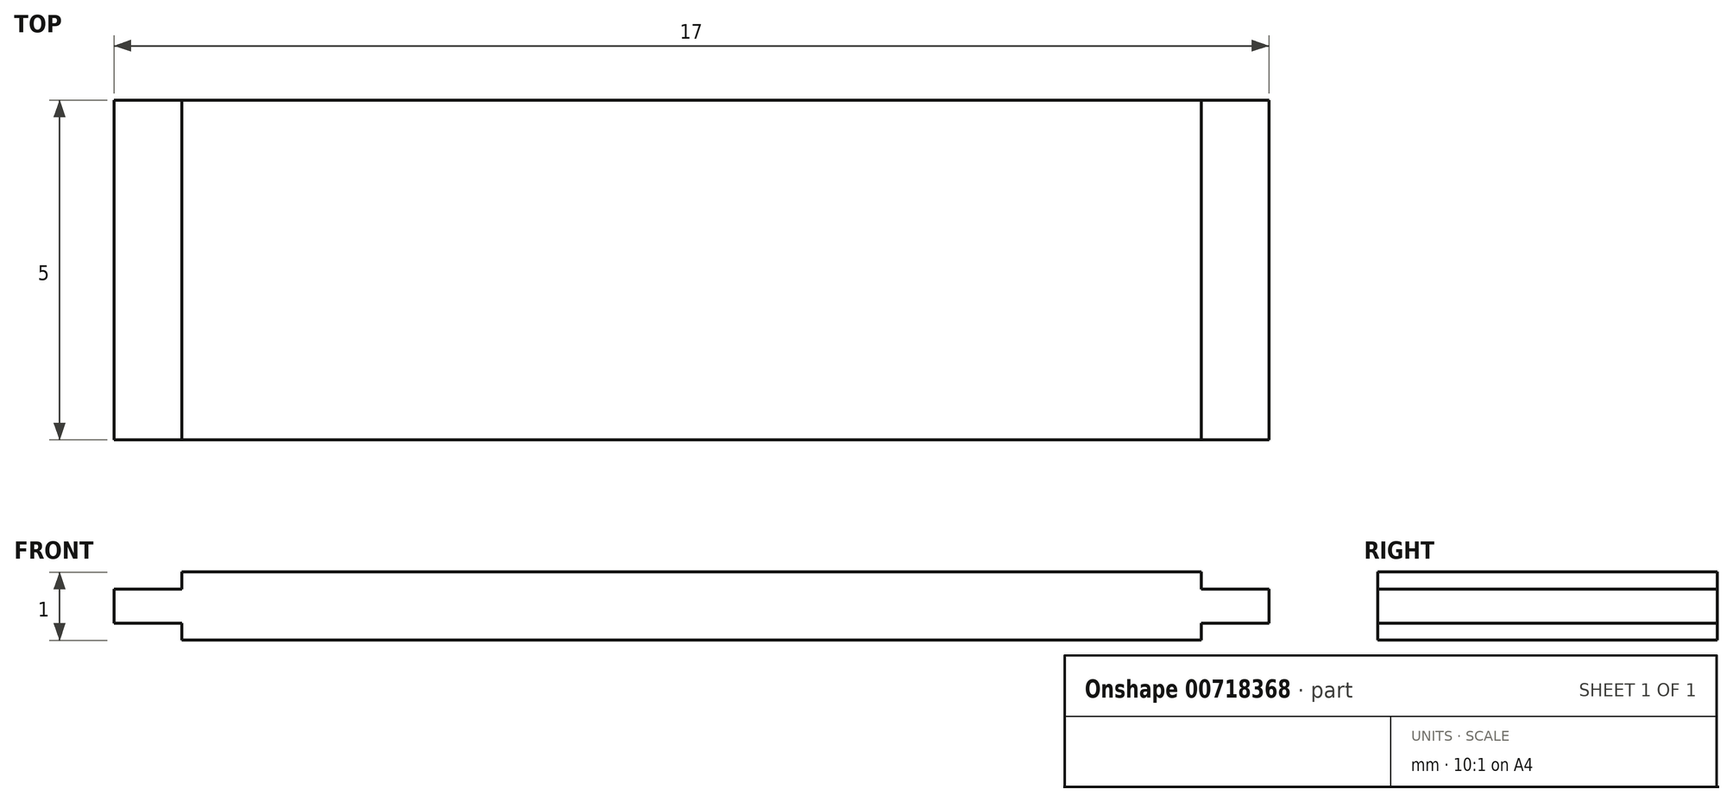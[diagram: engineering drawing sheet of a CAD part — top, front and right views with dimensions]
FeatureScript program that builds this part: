
annotation { "Feature Type Name" : "Feature", "Feature Type Description" : "" }
export const myFeature = defineFeature(function(context is Context, id is Id, definition is map)
    precondition{}
    {
        {
            var Q0;
            Q0=qCreatedBy(makeId("Front.planeOp"),FACE);
            var sketch = newSketch(context, id + "F0", { "sketchPlane" : qUnion([Q0])});
            skLineSegment(sketch, "E0.bottom", {"start": v(-2.69, -4.7) * mm, "end": v(-17.69, -4.7) * mm});
            skLineSegment(sketch, "E0.top", {"start": v(-2.69, -5.7) * mm, "end": v(-17.69, -5.7) * mm});
            skLineSegment(sketch, "E0.left", {"start": v(-2.69, -4.7) * mm, "end": v(-2.69, -5.7) * mm});
            skLineSegment(sketch, "E0.right", {"start": v(-17.69, -4.7) * mm, "end": v(-17.69, -5.7) * mm});
            skSolve(sketch);
        }
        {
            var Q0;
            Q0=makeQuery(id+"F0.imprint","IMPRINT",FACE,{"disambiguationData":[TD([[makeQuery(id+"F0.imprint","IMPRINT",EDGE,{"derivedFrom":sQuery(id+"F0.wireOp",EDGE,"E0.bottom")}),1.0]])]});
            extrude(context, id + "F1", {"entities" : qUnion([Q0]), "depth" : 5 * mm, "offsetDistance" : 25 * mm});
        }
        {
            var Q0;
            Q0=makeQuery(id+"F1.opExtrude","SWEPT_FACE",FACE,{"disambiguationData":[OSD([sQuery(id+"F0.wireOp",EDGE,"E0.right")])]});
            var sketch = newSketch(context, id + "F2", { "sketchPlane" : qUnion([Q0])});
            skLineSegment(sketch, "E1", {"start": v(0, -4.7) * mm, "end": v(0, -4.95) * mm});
            skLineSegment(sketch, "E2", {"start": v(0, -5.7) * mm, "end": v(0, -5.45) * mm});
            skLineSegment(sketch, "E3.bottom", {"start": v(0, -4.95) * mm, "end": v(5, -4.95) * mm});
            skLineSegment(sketch, "E3.top", {"start": v(0, -5.45) * mm, "end": v(5, -5.45) * mm});
            skLineSegment(sketch, "E3.left", {"start": v(0, -4.95) * mm, "end": v(0, -5.45) * mm});
            skLineSegment(sketch, "E3.right", {"start": v(5, -4.95) * mm, "end": v(5, -5.45) * mm});
            skSolve(sketch);
        }
        {
            var Q0;
            Q0=makeQuery(id+"F2.imprint","IMPRINT",FACE,{"disambiguationData":[TD([[makeQuery(id+"F2.imprint","IMPRINT",EDGE,{"derivedFrom":sQuery(id+"F2.wireOp",EDGE,"E3.bottom")}),-1.0]])]});
            extrude(context, id + "F3", {"entities" : qUnion([Q0]), "operationType" : NewBodyOperationType.ADD, "depth" : 1 * mm, "offsetDistance" : 25 * mm});
        }
        {
            var Q0;
            Q0=makeQuery(id+"F1.opExtrude","SWEPT_FACE",FACE,{"disambiguationData":[OSD([sQuery(id+"F0.wireOp",EDGE,"E0.left")])]});
            var sketch = newSketch(context, id + "F4", { "sketchPlane" : qUnion([Q0])});
            skLineSegment(sketch, "E4.bottom", {"start": v(-5, -4.95) * mm, "end": v(0, -4.95) * mm});
            skLineSegment(sketch, "E4.top", {"start": v(-5, -5.45) * mm, "end": v(0, -5.45) * mm});
            skLineSegment(sketch, "E4.left", {"start": v(-5, -4.95) * mm, "end": v(-5, -5.45) * mm});
            skLineSegment(sketch, "E4.right", {"start": v(0, -4.95) * mm, "end": v(0, -5.45) * mm});
            skSolve(sketch);
        }
        {
            var Q0;
            Q0=makeQuery(id+"F4.imprint","IMPRINT",FACE,{"disambiguationData":[TD([[makeQuery(id+"F4.imprint","IMPRINT",EDGE,{"derivedFrom":sQuery(id+"F4.wireOp",EDGE,"E4.bottom")}),-1.0]])]});
            extrude(context, id + "F5", {"entities" : qUnion([Q0]), "operationType" : NewBodyOperationType.ADD, "depth" : 1 * mm, "offsetDistance" : 25 * mm});
        }
    });
